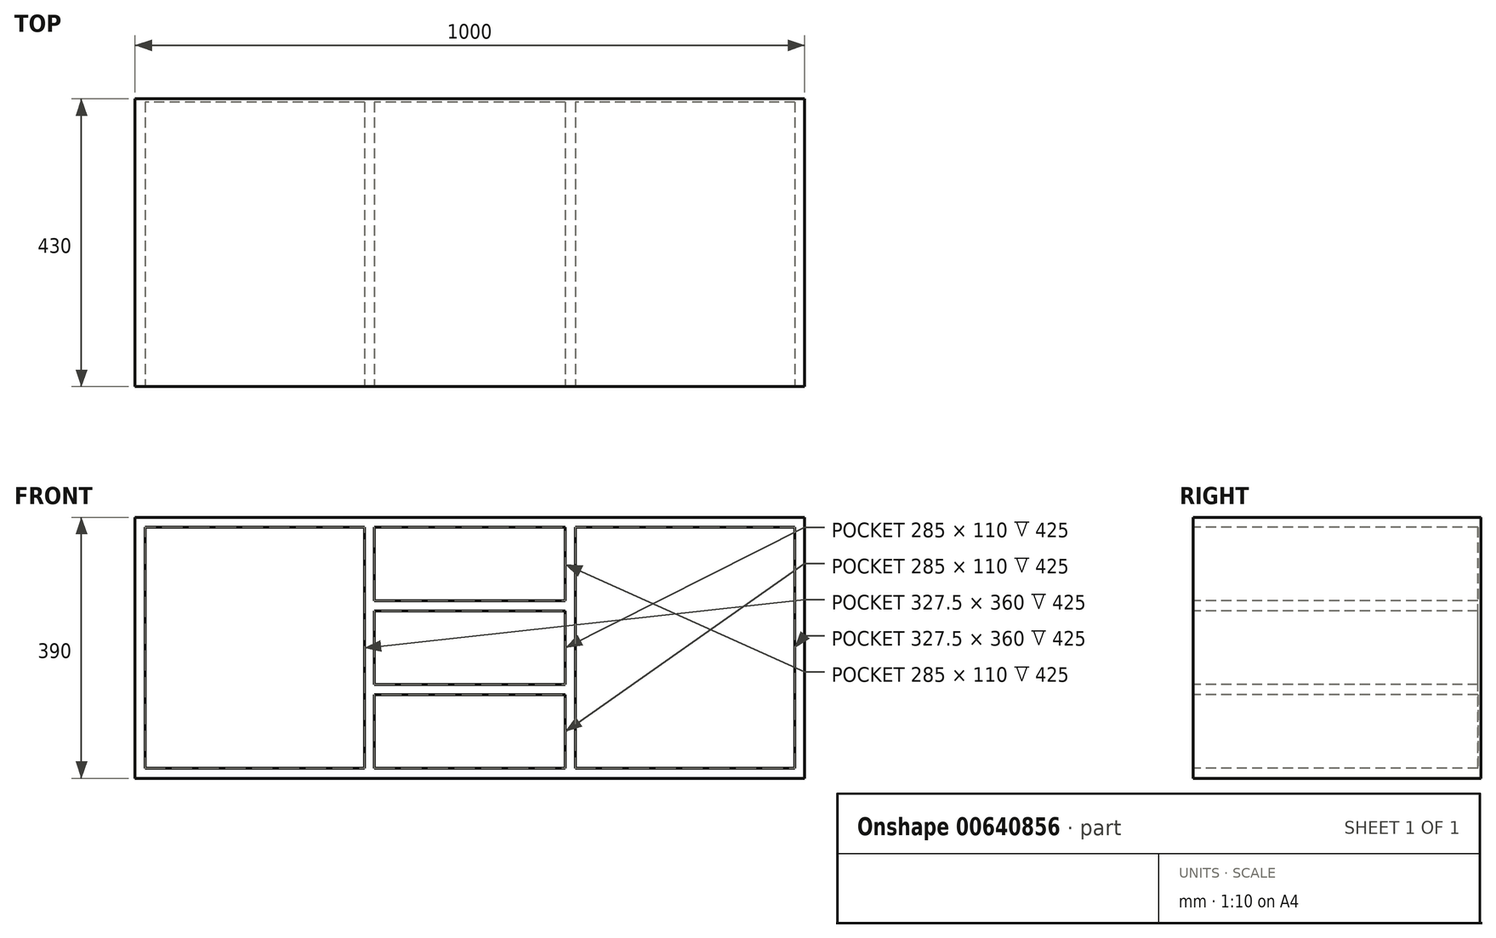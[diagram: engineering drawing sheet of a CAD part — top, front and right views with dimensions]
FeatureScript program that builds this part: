
annotation { "Feature Type Name" : "Feature", "Feature Type Description" : "" }
export const myFeature = defineFeature(function(context is Context, id is Id, definition is map)
    precondition{}
    {
        {
            var Q0;
            Q0=qCreatedBy(makeId("Top.planeOp"),FACE);
            var sketch = newSketch(context, id + "F0", { "sketchPlane" : qUnion([Q0])});
            skLineSegment(sketch, "E0.bottom", {"start": v(500, -215) * mm, "end": v(-500, -215) * mm});
            skLineSegment(sketch, "E0.top", {"start": v(500, 215) * mm, "end": v(-500, 215) * mm});
            skLineSegment(sketch, "E0.left", {"start": v(500, -215) * mm, "end": v(500, 215) * mm});
            skLineSegment(sketch, "E0.right", {"start": v(-500, -215) * mm, "end": v(-500, 215) * mm});
            skPoint(sketch, "E0.middle", {"position": v(0, 0) * mm});
            skSolve(sketch);
        }
        {
            var Q0;
            Q0=makeQuery(id+"F0.imprint","IMPRINT",FACE,{"disambiguationData":[TD([[makeQuery(id+"F0.imprint","IMPRINT",EDGE,{"derivedFrom":sQuery(id+"F0.wireOp",EDGE,"E0.bottom")}),-1.0]])]});
            extrude(context, id + "F1", {"entities" : qUnion([Q0]), "depth" : 390 * mm, "offsetDistance" : 25 * mm});
        }
        {
            var Q0;
            Q0=makeQuery(id+"F1.opExtrude","SWEPT_FACE",FACE,{"disambiguationData":[OSD([sQuery(id+"F0.wireOp",EDGE,"E0.bottom")])]});
            var sketch = newSketch(context, id + "F2", { "sketchPlane" : qUnion([Q0])});
            skPoint(sketch, "E1.middle", {"position": v(0, 195) * mm});
            skLineSegment(sketch, "E2.bottom", {"start": v(-157.5, 15) * mm, "end": v(-485, 15) * mm});
            skLineSegment(sketch, "E2.top", {"start": v(-157.5, 375) * mm, "end": v(-485, 375) * mm});
            skLineSegment(sketch, "E2.left", {"start": v(-157.5, 15) * mm, "end": v(-157.5, 375) * mm});
            skLineSegment(sketch, "E2.right", {"start": v(-485, 15) * mm, "end": v(-485, 375) * mm});
            skPoint(sketch, "E2.middle", {"position": v(-321.25, 195) * mm});
            skLineSegment(sketch, "E3.bottom", {"start": v(485, 15) * mm, "end": v(157.5, 15) * mm});
            skLineSegment(sketch, "E3.top", {"start": v(485, 375) * mm, "end": v(157.5, 375) * mm});
            skLineSegment(sketch, "E3.left", {"start": v(485, 15) * mm, "end": v(485, 375) * mm});
            skLineSegment(sketch, "E3.right", {"start": v(157.5, 15) * mm, "end": v(157.5, 375) * mm});
            skPoint(sketch, "E3.middle", {"position": v(321.25, 195) * mm});
            skPoint(sketch, "E3.middle.positionSnap0", {"position": v(142.5, 195) * mm});
            skPoint(sketch, "E3.centerSnap0", {"position": v(142.5, 195) * mm});
            skLineSegment(sketch, "E4.bottom", {"start": v(142.5, 140) * mm, "end": v(-142.5, 140) * mm});
            skLineSegment(sketch, "E4.top", {"start": v(142.5, 250) * mm, "end": v(-142.5, 250) * mm});
            skLineSegment(sketch, "E4.left", {"start": v(142.5, 140) * mm, "end": v(142.5, 250) * mm});
            skLineSegment(sketch, "E4.right", {"start": v(-142.5, 140) * mm, "end": v(-142.5, 250) * mm});
            skLineSegment(sketch, "E5.MirrorCS", {"start": v(142.5, 265) * mm, "end": v(-142.5, 265) * mm});
            skLineSegment(sketch, "E6.MirrorCS", {"start": v(-142.5, 375) * mm, "end": v(-142.5, 265) * mm});
            skLineSegment(sketch, "E7.MirrorCS", {"start": v(142.5, 375) * mm, "end": v(142.5, 265) * mm});
            skLineSegment(sketch, "E8.MirrorCS", {"start": v(142.5, 375) * mm, "end": v(-142.5, 375) * mm});
            skLineSegment(sketch, "E9.MirrorCS", {"start": v(142.5, 125) * mm, "end": v(-142.5, 125) * mm});
            skLineSegment(sketch, "E10.MirrorCS", {"start": v(142.5, 15) * mm, "end": v(-142.5, 15) * mm});
            skLineSegment(sketch, "E11.MirrorCS", {"start": v(-142.5, 125) * mm, "end": v(-142.5, 15) * mm});
            skLineSegment(sketch, "E12.MirrorCS", {"start": v(142.5, 125) * mm, "end": v(142.5, 15) * mm});
            skSolve(sketch);
        }
        {
            var Q0;
            Q0=makeQuery(id+"F2.imprint","IMPRINT",FACE,{"disambiguationData":[TD([[makeQuery(id+"F2.imprint","IMPRINT",EDGE,{"derivedFrom":sQuery(id+"F2.wireOp",EDGE,"E4.bottom")}),-1.0]])]});
            var Q1;
            Q1=makeQuery(id+"F2.imprint","IMPRINT",FACE,{"disambiguationData":[TD([[makeQuery(id+"F2.imprint","IMPRINT",EDGE,{"derivedFrom":sQuery(id+"F2.wireOp",EDGE,"E5.MirrorCS")}),-1.0]])]});
            var Q2;
            Q2=makeQuery(id+"F2.imprint","IMPRINT",FACE,{"disambiguationData":[TD([[makeQuery(id+"F2.imprint","IMPRINT",EDGE,{"derivedFrom":sQuery(id+"F2.wireOp",EDGE,"E3.bottom")}),-1.0]])]});
            var Q3;
            Q3=makeQuery(id+"F2.imprint","IMPRINT",FACE,{"disambiguationData":[TD([[makeQuery(id+"F2.imprint","IMPRINT",EDGE,{"derivedFrom":sQuery(id+"F2.wireOp",EDGE,"E2.bottom")}),-1.0]])]});
            var Q4;
            Q4=makeQuery(id+"F2.imprint","IMPRINT",FACE,{"disambiguationData":[TD([[makeQuery(id+"F2.imprint","IMPRINT",EDGE,{"derivedFrom":sQuery(id+"F2.wireOp",EDGE,"E9.MirrorCS")}),1.0]])]});
            extrude(context, id + "F3", {"entities" : qUnion([Q0, Q1, Q2, Q3, Q4]), "operationType" : NewBodyOperationType.REMOVE, "oppositeDirection" : true, "depth" : 425 * mm, "offsetDistance" : 25 * mm});
        }
    });
